# Revit family: Dallmeier_Fisheye_Cameras_en
name_source: partatom
category: Sicherheitsgeräte
units: mm (PartAtom-declared; Revit-internal decimal feet)

## family parameters
Basisbauteil = Fläche
Beim Laden mit Abzugskörper schneiden = Nein
Bemaßung runder Anschluss = Durchmesser verwenden
Beschriftungsausrichtung beibehalten = Nein
Gemeinsam genutzt = Nein
Raumberechnungspunkt = Nein
Teiletyp = Normal

## types (2) — shared parameters
FOV Length Anpassung Horizontal = 36,65°
FOV Length Anpassung Vertical = 90,00°
Hersteller = Dallmeier electronic GmbH
URL = https://www.dallmeier.com
Vorgabe-Ansicht = 122 cm
number of sensors = 1
operating temperature = -20°C to +50°C
power consumption = 12 W
voltage supply = 24 V

## per-type parameters (varying)
| type | Modell | Show_MDF | Show_SDF | dimensions | weight |
| MDF 5450 HD-DN | Dallmeier Fisheye MDF 5450 | Ja | Nein | Ø95x49mm | 0,27 kg |
| SDF 5450 HD-DN | Dallmeier Fisheye SDF 5450 | Nein | Ja | Ø151x64mm | 0,50 kg |

## geometry (parser evidence)
native form markers: Sweep x10
no freeform markers — native parametric forms only
